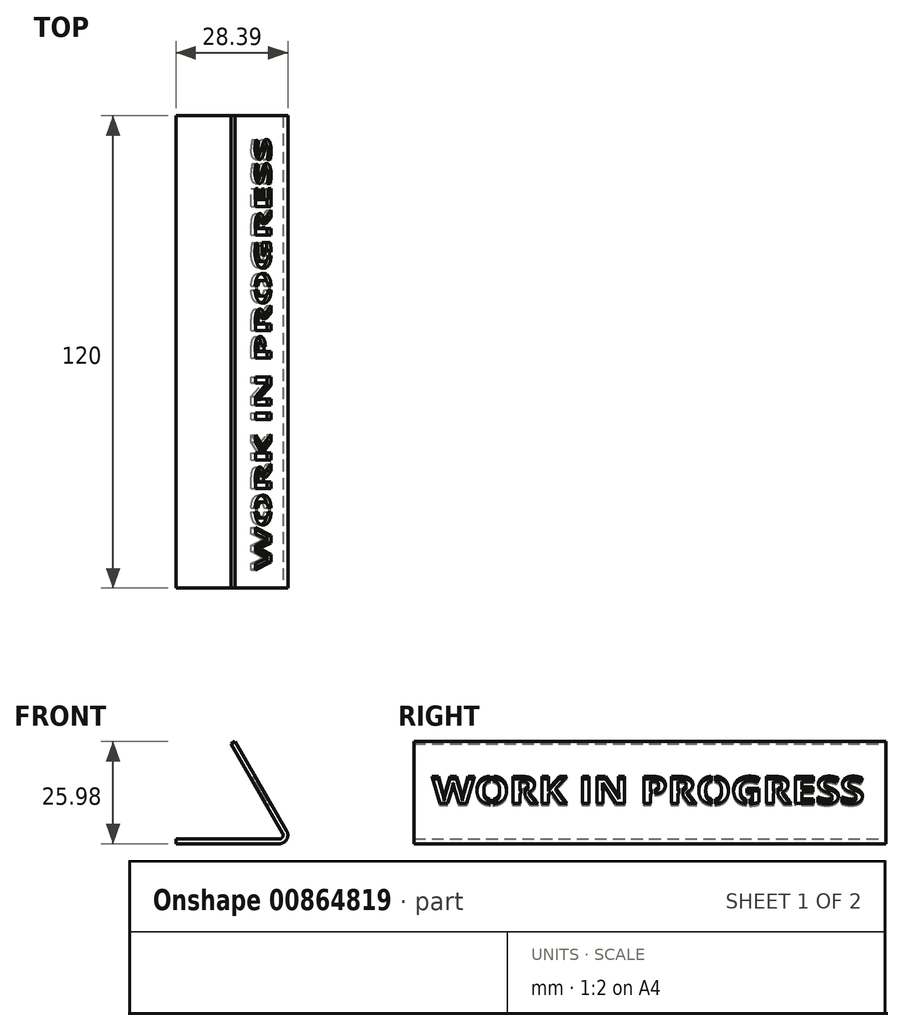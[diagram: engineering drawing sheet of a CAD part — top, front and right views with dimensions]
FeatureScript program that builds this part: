
annotation { "Feature Type Name" : "Feature", "Feature Type Description" : "" }
export const myFeature = defineFeature(function(context is Context, id is Id, definition is map)
    precondition{}
    {
        {
            var Q0;
            Q0=qCreatedBy(makeId("Front.planeOp"),FACE);
            var sketch = newSketch(context, id + "F0", { "sketchPlane" : qUnion([Q0])});
            skLineSegment(sketch, "E0", {"start": v(0, 0) * mm, "end": v(30, 0) * mm});
            skLineSegment(sketch, "E1", {"start": v(30, 0) * mm, "end": v(15, 25.98) * mm});
            skLineSegment(sketch, "E2", {"start": v(15, 25.98) * mm, "end": v(13.96, 25.38) * mm});
            skLineSegment(sketch, "E3", {"start": v(13.96, 25.38) * mm, "end": v(27.92, 1.2) * mm});
            skLineSegment(sketch, "E4", {"start": v(27.92, 1.2) * mm, "end": v(0, 1.2) * mm});
            skLineSegment(sketch, "E5", {"start": v(0, 1.2) * mm, "end": v(0, 0) * mm});
            skSolve(sketch);
        }
        {
            var Q0;
            Q0 = qSketchRegion(id + "F0", true);
            extrude(context, id + "F1", {"entities" : qUnion([Q0]), "depth" : 120 * mm, "offsetDistance" : 25 * mm});
        }
        {
            var Q0;
            Q0 = qSketchRegion(id + "F0", true);
            extrude(context, id + "F2", {"entities" : qUnion([Q0]), "operationType" : NewBodyOperationType.ADD, "depth" : 120 * mm, "offsetDistance" : 25 * mm});
        }
        {
            var Q0;
            Q0=makeQuery(id+"F1.opExtrude","SWEPT_EDGE",EDGE,{"disambiguationData":[OSD([sQuery(id+"F0.wireOp",EDGE,"E3"),sQuery(id+"F0.wireOp",EDGE,"E4")])]});
            fillet(context, id + "F3", {"entities" : qUnion([Q0]), "radius" : 1 * mm, "tangentPropagation" : true, "allowEdgeOverflow" : false});
        }
        {
            var Q0;
            Q0=makeQuery(id+"F1.opExtrude","SWEPT_EDGE",EDGE,{"disambiguationData":[OSD([sQuery(id+"F0.wireOp",EDGE,"E0"),sQuery(id+"F0.wireOp",EDGE,"E1")])]});
            fillet(context, id + "F4", {"entities" : qUnion([Q0]), "radius" : 2.2 * mm, "tangentPropagation" : true, "allowEdgeOverflow" : false});
        }
        {
            var Q0;
            Q0=makeQuery(id+"F1.opExtrude","SWEPT_FACE",FACE,{"disambiguationData":[OSD([sQuery(id+"F0.wireOp",EDGE,"E1")])]});
            var sketch = newSketch(context, id + "F5", { "sketchPlane" : qUnion([Q0])});
            skLineSegment(sketch, "E6.bottom", {"start": v(-100.76, 8.81) * mm, "end": v(-19.24, 8.81) * mm});
            skLineSegment(sketch, "E6.top", {"start": v(-100.76, -8.19) * mm, "end": v(-19.24, -8.19) * mm});
            skLineSegment(sketch, "E6.left", {"start": v(-100.76, 8.81) * mm, "end": v(-100.76, -8.19) * mm});
            skLineSegment(sketch, "E6.right", {"start": v(-19.24, 8.81) * mm, "end": v(-19.24, -8.19) * mm});
            skLineSegment(sketch, "E7", {"start": v(-60, -8.19) * mm, "end": v(-60, -11.19) * mm});
            skSolve(sketch);
        }
        {
            var Q0;
            Q0=makeQuery(id+"F5.imprint","IMPRINT",FACE,{"disambiguationData":[TD([[makeQuery(id+"F5.imprint","IMPRINT",EDGE,{"derivedFrom":sQuery(id+"F5.wireOp",EDGE,"E6.bottom")}),1.0]])]});
            var sketch = newSketch(context, id + "F6", { "sketchPlane" : qUnion([Q0])});
            skText(sketch, "E8", { "text": "WORK IN PROGRESS", "fontName": "OpenSans-Bold.ttf"});
            const initialGuessF6  = {"E8": [-0.11535, -0.00319, 1, 0, 0.008]};
            skSetInitialGuess(sketch, initialGuessF6);
            skSolve(sketch);
        }
        {
            var Q0;
            Q0 = qSketchRegion(id + "F6", true);
            extrude(context, id + "F7", {"entities" : qUnion([Q0]), "operationType" : NewBodyOperationType.REMOVE, "oppositeDirection" : true, "depth" : 5 * mm, "offsetDistance" : 25 * mm});
        }
        {
            var Q0;
            Q0=makeQuery(id+"F6.imprint","IMPRINT",FACE,{"disambiguationData":[TD([[makeQuery(id+"F6.imprint","IMPRINT",EDGE,{"derivedFrom":sQuery(id+"F6.wireOp",EDGE,"E8.sketch_text.stroke-0")}),1.0]])]});
            var sketch = newSketch(context, id + "F8", { "sketchPlane" : qUnion([Q0])});
            skLineSegment(sketch, "E9.bottom", {"start": v(-100.7, 6.22) * mm, "end": v(-99.7, 6.22) * mm});
            skLineSegment(sketch, "E9.top", {"start": v(-100.7, -5.85) * mm, "end": v(-99.7, -5.85) * mm});
            skLineSegment(sketch, "E9.left", {"start": v(-100.7, 6.22) * mm, "end": v(-100.7, -5.85) * mm});
            skLineSegment(sketch, "E9.right", {"start": v(-99.7, 6.22) * mm, "end": v(-99.7, -5.85) * mm});
            skLineSegment(sketch, "E10.bottom", {"start": v(-92.74, 2.8) * mm, "end": v(-91.74, 2.8) * mm});
            skLineSegment(sketch, "E10.top", {"start": v(-92.74, -3.57) * mm, "end": v(-91.74, -3.57) * mm});
            skLineSegment(sketch, "E10.left", {"start": v(-92.74, 2.8) * mm, "end": v(-92.74, -3.57) * mm});
            skLineSegment(sketch, "E10.right", {"start": v(-91.74, 2.8) * mm, "end": v(-91.74, -3.57) * mm});
            skLineSegment(sketch, "E11.bottom", {"start": v(-59.6, 2.2) * mm, "end": v(-58.6, 2.2) * mm});
            skLineSegment(sketch, "E11.top", {"start": v(-59.6, -2.5) * mm, "end": v(-58.6, -2.5) * mm});
            skLineSegment(sketch, "E11.left", {"start": v(-59.6, 2.2) * mm, "end": v(-59.6, -2.5) * mm});
            skLineSegment(sketch, "E11.right", {"start": v(-58.6, 2.2) * mm, "end": v(-58.6, -2.5) * mm});
            skLineSegment(sketch, "E12.bottom", {"start": v(-52.59, 1.9) * mm, "end": v(-51.59, 1.9) * mm});
            skLineSegment(sketch, "E12.top", {"start": v(-52.59, -2.09) * mm, "end": v(-51.59, -2.09) * mm});
            skLineSegment(sketch, "E12.left", {"start": v(-52.59, 1.9) * mm, "end": v(-52.59, -2.09) * mm});
            skLineSegment(sketch, "E12.right", {"start": v(-51.59, 1.9) * mm, "end": v(-51.59, -2.09) * mm});
            skLineSegment(sketch, "E13.bottom", {"start": v(-44.34, 5.55) * mm, "end": v(-43.34, 5.55) * mm});
            skLineSegment(sketch, "E13.top", {"start": v(-44.34, -4.66) * mm, "end": v(-43.34, -4.66) * mm});
            skLineSegment(sketch, "E13.left", {"start": v(-44.34, 5.55) * mm, "end": v(-44.34, -4.66) * mm});
            skLineSegment(sketch, "E13.right", {"start": v(-43.34, 5.55) * mm, "end": v(-43.34, -4.66) * mm});
            skLineSegment(sketch, "E14.bottom", {"start": v(-28.46, 1.55) * mm, "end": v(-27.46, 1.55) * mm});
            skLineSegment(sketch, "E14.top", {"start": v(-28.46, -2.24) * mm, "end": v(-27.46, -2.24) * mm});
            skLineSegment(sketch, "E14.left", {"start": v(-28.46, 1.55) * mm, "end": v(-28.46, -2.24) * mm});
            skLineSegment(sketch, "E14.right", {"start": v(-27.46, 1.55) * mm, "end": v(-27.46, -2.24) * mm});
            skLineSegment(sketch, "E15.bottom", {"start": v(-35.59, -1.34) * mm, "end": v(-34.59, -1.34) * mm});
            skLineSegment(sketch, "E15.top", {"start": v(-35.59, -3.9) * mm, "end": v(-34.59, -3.9) * mm});
            skLineSegment(sketch, "E15.left", {"start": v(-35.59, -1.34) * mm, "end": v(-35.59, -3.9) * mm});
            skLineSegment(sketch, "E15.right", {"start": v(-34.59, -1.34) * mm, "end": v(-34.59, -3.9) * mm});
            skSolve(sketch);
        }
        {
            var Q0;
            Q0 = qSketchRegion(id + "F8", true);
            extrude(context, id + "F9", {"entities" : qUnion([Q0]), "operationType" : NewBodyOperationType.ADD, "oppositeDirection" : true, "depth" : 1.2 * mm, "offsetDistance" : 25 * mm});
        }
    });
